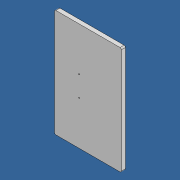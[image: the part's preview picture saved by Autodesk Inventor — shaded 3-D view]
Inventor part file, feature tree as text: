
AUTODESK INVENTOR PART (.ipt)
format: ipt  version: 2020 (Build 240168000, 168)  size: 109,056 bytes
history: native  units: mm
features: sketch x3, extrude x2, other x1, hole x1, fillet x1, projected_geometry x1
ambient origin geometry x8: Origin, YZ Plane, XZ Plane, XY Plane, X Axis, Y Axis, Z Axis, Center Point
bodies: Body1 (feature_tree)
feature tree (9):
  other  "ソリッド1"
  extrude  "押し出し1"  Depth=245.0mm
  hole  "穴1"  [1 undecoded]
  extrude  "押し出し2"  Depth=15.0mm TaperAngle=0.0deg
  fillet  "フィレット1"  Radius=90.0mm
  sketch  "スケッチ1"
  sketch  "スケッチ2"
  sketch  "スケッチ3"
  projected_geometry  "投影ループ1"
note: 1 required parameter value undecoded (feature->parameter linkage not recoverable at this tier; creation-order binding heuristic only, values carry confidence <= 0.55)
